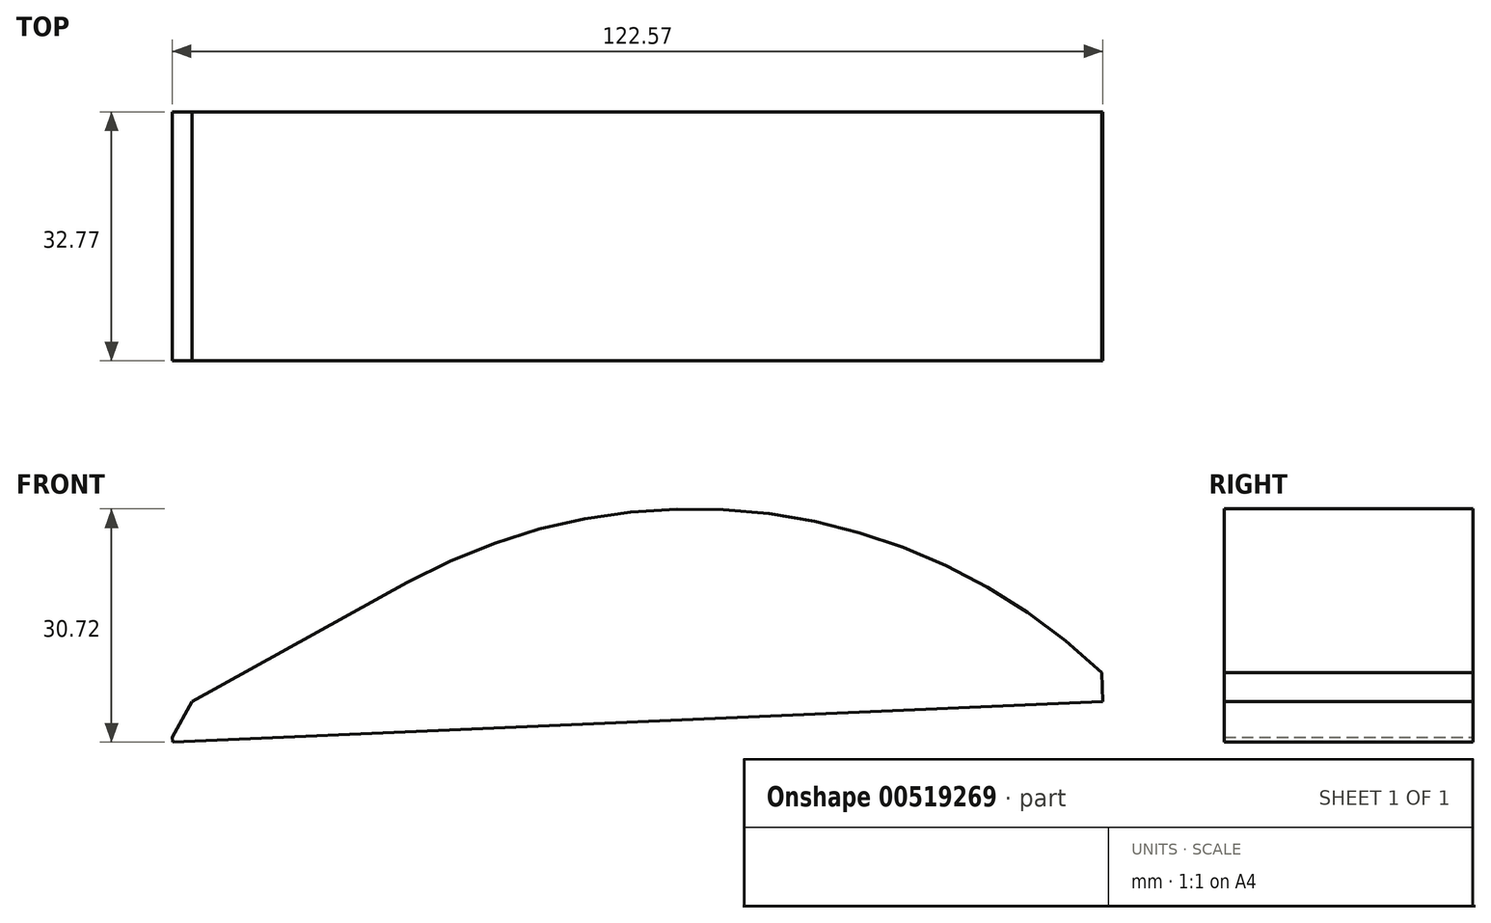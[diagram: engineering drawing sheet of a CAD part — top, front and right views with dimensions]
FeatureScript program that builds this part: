
annotation { "Feature Type Name" : "Feature", "Feature Type Description" : "" }
export const myFeature = defineFeature(function(context is Context, id is Id, definition is map)
    precondition{}
    {
        {
            var Q0;
            Q0=qCreatedBy(makeId("Front.planeOp"),FACE);
            var sketch = newSketch(context, id + "F0", { "sketchPlane" : qUnion([Q0])});
            skLineSegment(sketch, "E0", {"start": v(57.87, 62.53) * mm, "end": v(-64.67, -5.32) * mm});
            skLineSegment(sketch, "E1", {"start": v(-64.67, -5.32) * mm, "end": v(57.87, 0) * mm});
            skLineSegment(sketch, "E2", {"start": v(57.87, 0) * mm, "end": v(57.87, 62.53) * mm});
            skSolve(sketch);
        }
        {
            var Q0;
            Q0=makeQuery(id+"F0.imprint","IMPRINT",FACE,{"disambiguationData":[TD([[makeQuery(id+"F0.imprint","IMPRINT",EDGE,{"derivedFrom":sQuery(id+"F0.wireOp",EDGE,"E0")}),1.0]])]});
            extrude(context, id + "F1", {"entities" : qUnion([Q0]), "depth" : 32.77 * mm, "offsetDistance" : 25.4 * mm});
        }
        {
            var Q0;
            Q0=makeQuery(id+"F1.opExtrude","SWEPT_EDGE",EDGE,{"disambiguationData":[OSD([sQuery(id+"F0.wireOp",EDGE,"E0"),sQuery(id+"F0.wireOp",EDGE,"E2")])]});
            fillet(context, id + "F2", {"entities" : qUnion([Q0]), "radius" : 77.82 * mm, "tangentPropagation" : true, "allowEdgeOverflow" : false});
        }
        {
            var Q0;
            Q0=makeQuery(id+"F1.opExtrude","SWEPT_FACE",FACE,{"disambiguationData":[OSD([sQuery(id+"F0.wireOp",EDGE,"E1")])]});
            extrude(context, id + "F3", {"entities" : qUnion([Q0]), "operationType" : NewBodyOperationType.ADD, "depth" : 3.8 * mm, "offsetDistance" : 25.4 * mm});
        }
        {
            var Q0;
            {var subQ0=sQuery(id+"F0.wireOp",EDGE,"E1");var subQ1=sQuery(id+"F0.wireOp",EDGE,"E0");Q0=makeQuery(id+"F3.boolean.opBoolean","MERGE",EDGE,{"derivedFrom":[makeQuery(id+"F1.opExtrude","SWEPT_EDGE",EDGE,{"disambiguationData":[OSD([subQ1,subQ0])]}),makeQuery(id+"F3.opExtrude","CAP_EDGE",EDGE,{"disambiguationData":[OSD([subQ1,subQ0])],"isStart":true})]});}
            chamfer(context, id + "F4", {"entities" : qUnion([Q0]), "width" : 5.08 * mm, "tangentPropagation" : true});
        }
    });
